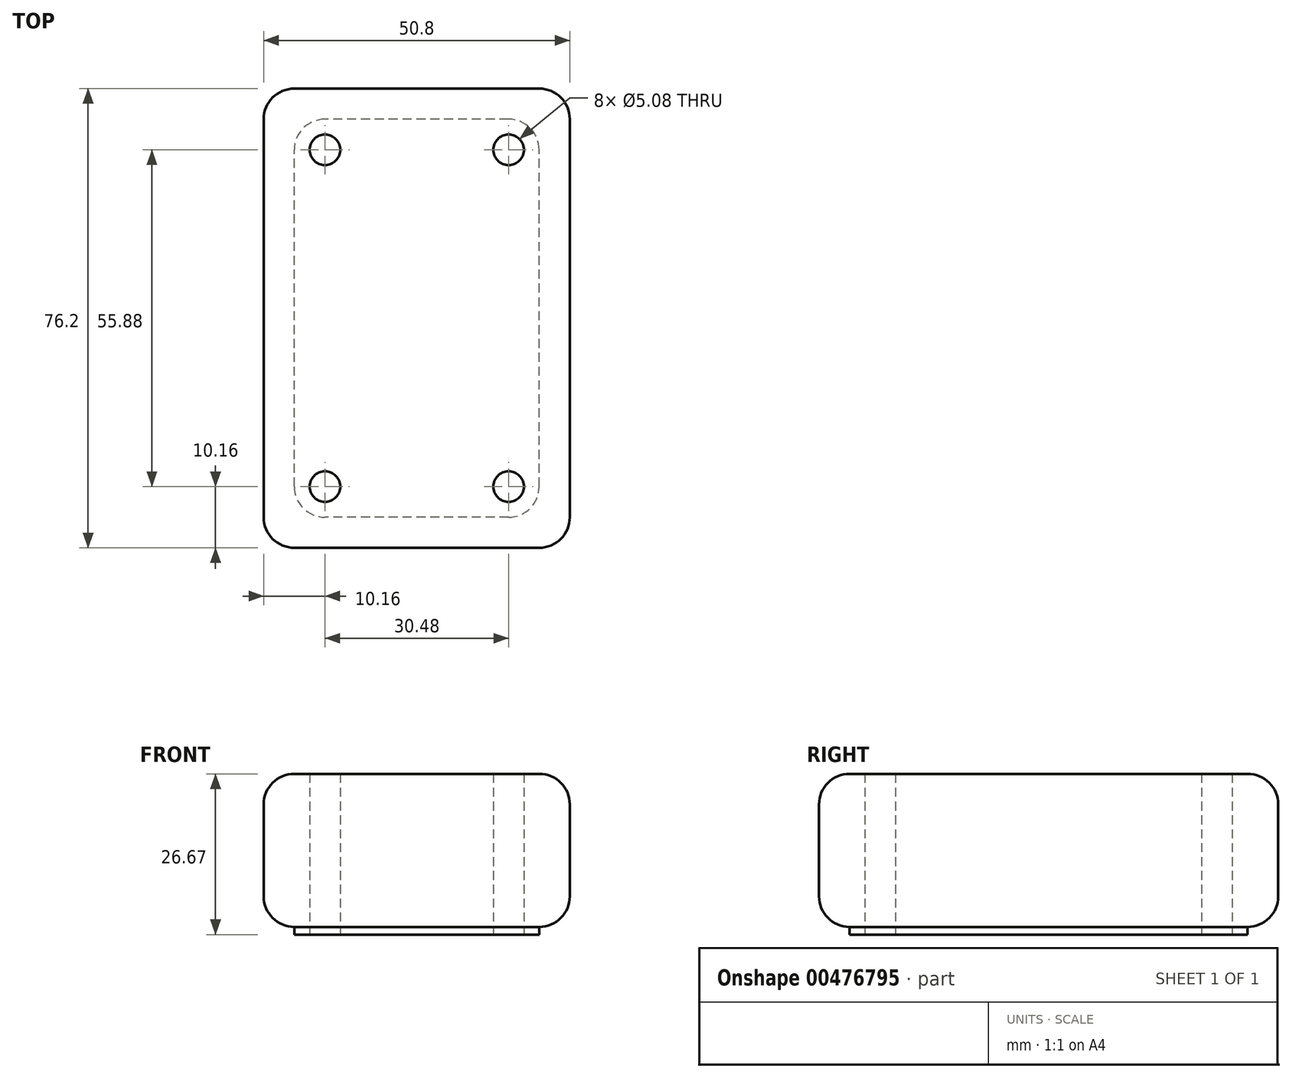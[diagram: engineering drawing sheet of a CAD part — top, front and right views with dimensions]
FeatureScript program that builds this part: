
annotation { "Feature Type Name" : "Feature", "Feature Type Description" : "" }
export const myFeature = defineFeature(function(context is Context, id is Id, definition is map)
    precondition{}
    {
        {
            var Q0;
            Q0=qCreatedBy(makeId("Front.planeOp"),FACE);
            var sketch = newSketch(context, id + "F0", { "sketchPlane" : qUnion([Q0])});
            skLineSegment(sketch, "E0.bottom", {"start": v(25.4, 12.7) * mm, "end": v(-25.4, 12.7) * mm});
            skLineSegment(sketch, "E0.top", {"start": v(25.4, -12.7) * mm, "end": v(-25.4, -12.7) * mm});
            skLineSegment(sketch, "E0.left", {"start": v(25.4, 12.7) * mm, "end": v(25.4, -12.7) * mm});
            skLineSegment(sketch, "E0.right", {"start": v(-25.4, 12.7) * mm, "end": v(-25.4, -12.7) * mm});
            skPoint(sketch, "E0.middle", {"position": v(0, 0) * mm});
            skSolve(sketch);
        }
        {
            var Q0;
            Q0 = qSketchRegion(id + "F0", true);
            extrude(context, id + "F1", {"entities" : qUnion([Q0]), "depth" : 76.2 * mm});
        }
        {
            var Q0;
            Q0=makeQuery(id+"F1.opExtrude","SWEPT_EDGE",EDGE,{"disambiguationData":[OSD([sQuery(id+"F0.wireOp",EDGE,"E0.bottom"),sQuery(id+"F0.wireOp",EDGE,"E0.left")])]});
            var Q1;
            Q1=makeQuery(id+"F1.opExtrude","CAP_EDGE",EDGE,{"disambiguationData":[OSD([sQuery(id+"F0.wireOp",EDGE,"E0.bottom")])],"isStart":true});
            var Q2;
            Q2=makeQuery(id+"F1.opExtrude","SWEPT_EDGE",EDGE,{"disambiguationData":[OSD([sQuery(id+"F0.wireOp",EDGE,"E0.bottom"),sQuery(id+"F0.wireOp",EDGE,"E0.right")])]});
            var Q3;
            Q3=makeQuery(id+"F1.opExtrude","SWEPT_EDGE",EDGE,{"disambiguationData":[OSD([sQuery(id+"F0.wireOp",EDGE,"E0.top"),sQuery(id+"F0.wireOp",EDGE,"E0.left")])]});
            var Q4;
            Q4=makeQuery(id+"F1.opExtrude","SWEPT_EDGE",EDGE,{"disambiguationData":[OSD([sQuery(id+"F0.wireOp",EDGE,"E0.top"),sQuery(id+"F0.wireOp",EDGE,"E0.right")])]});
            var Q5;
            Q5=makeQuery(id+"F1.opExtrude","CAP_EDGE",EDGE,{"disambiguationData":[OSD([sQuery(id+"F0.wireOp",EDGE,"E0.top")])],"isStart":true});
            fillet(context, id + "F2", {"entities" : qUnion([Q0, Q1, Q2, Q3, Q4, Q5]), "radius" : 5.08 * mm, "tangentPropagation" : true, "allowEdgeOverflow" : false});
        }
        {
            var Q0;
            {var subQ0=sQuery(id+"F0.wireOp",EDGE,"E0.bottom");Q0=makeQuery(id+"F2.opFillet","BLEND_EDGE",EDGE,{"blendedFrom":[makeQuery(id+"F1.opExtrude","CAP_EDGE",EDGE,{"disambiguationData":[OSD([subQ0])],"isStart":true}),makeQuery(id+"F1.opExtrude","SWEPT_EDGE",EDGE,{"disambiguationData":[OSD([subQ0,sQuery(id+"F0.wireOp",EDGE,"E0.left")])]})],"blendedInto":[]});}
            var Q1;
            {var subQ0=sQuery(id+"F0.wireOp",EDGE,"E0.bottom");Q1=makeQuery(id+"F2.opFillet","BLEND_EDGE",EDGE,{"blendedFrom":[makeQuery(id+"F1.opExtrude","SWEPT_EDGE",EDGE,{"disambiguationData":[OSD([subQ0,sQuery(id+"F0.wireOp",EDGE,"E0.right")])]}),makeQuery(id+"F1.opExtrude","CAP_EDGE",EDGE,{"disambiguationData":[OSD([subQ0])],"isStart":true})],"blendedInto":[]});}
            var Q2;
            {var subQ0=sQuery(id+"F0.wireOp",EDGE,"E0.bottom");Q2=makeQuery(id+"F2.opFillet","BLEND_EDGE",EDGE,{"blendedFrom":[makeQuery(id+"F1.opExtrude","SWEPT_EDGE",EDGE,{"disambiguationData":[OSD([subQ0,sQuery(id+"F0.wireOp",EDGE,"E0.right")])]}),makeQuery(id+"F1.opExtrude","CAP_EDGE",EDGE,{"disambiguationData":[OSD([subQ0])],"isStart":false})],"blendedInto":[]});}
            fillet(context, id + "F3", {"entities" : qUnion([Q0, Q1, Q2]), "radius" : 5.08 * mm, "tangentPropagation" : true, "allowEdgeOverflow" : false});
        }
        {
            var Q0;
            {var subQ0=sQuery(id+"F0.wireOp",EDGE,"E0.left");var subQ1=sQuery(id+"F0.wireOp",EDGE,"E0.bottom");Q0=makeQuery(id+"F2.opFillet","BLEND_EDGE",EDGE,{"blendedFrom":[makeQuery(id+"F1.opExtrude","SWEPT_EDGE",EDGE,{"disambiguationData":[OSD([subQ1,subQ0])]}),makeQuery(id+"F1.opExtrude","CAP_FACE",FACE,{"disambiguationData":[OSD([subQ1,sQuery(id+"F0.wireOp",EDGE,"E0.top"),subQ0,sQuery(id+"F0.wireOp",EDGE,"E0.right")])],"isStart":false})],"blendedInto":[makeQuery(id+"F1.opExtrude","CAP_FACE",FACE,{"disambiguationData":[OSD([subQ1,sQuery(id+"F0.wireOp",EDGE,"E0.top"),subQ0,sQuery(id+"F0.wireOp",EDGE,"E0.right")])],"isStart":false})]});}
            fillet(context, id + "F4", {"entities" : qUnion([Q0]), "radius" : 5.08 * mm, "tangentPropagation" : true, "allowEdgeOverflow" : false});
        }
        {
            var Q0;
            Q0=makeQuery(id+"F1.opExtrude","SWEPT_FACE",FACE,{"disambiguationData":[OSD([sQuery(id+"F0.wireOp",EDGE,"E0.top")])]});
            var sketch = newSketch(context, id + "F5", { "sketchPlane" : qUnion([Q0])});
            skLineSegment(sketch, "E1.0", {"start": v(-20.32, 5.08) * mm, "end": v(20.32, 5.08) * mm});
            skLineSegment(sketch, "E2.0", {"start": v(20.32, 5.08) * mm, "end": v(20.32, 71.12) * mm});
            skLineSegment(sketch, "E3.0", {"start": v(20.32, 71.12) * mm, "end": v(-20.32, 71.12) * mm});
            skLineSegment(sketch, "E4.0", {"start": v(-20.32, 71.12) * mm, "end": v(-20.32, 5.08) * mm});
            skSolve(sketch);
        }
        {
            var Q0;
            Q0 = qSketchRegion(id + "F5", true);
            extrude(context, id + "F6", {"entities" : qUnion([Q0]), "depth" : 1.27 * mm});
        }
        {
            var Q0;
            Q0=makeQuery(id+"F6.opExtrude","SWEPT_EDGE",EDGE,{"disambiguationData":[OSD([sQuery(id+"F5.wireOp",EDGE,"E1.0"),sQuery(id+"F5.wireOp",EDGE,"E4.0")])]});
            var Q1;
            Q1=makeQuery(id+"F6.opExtrude","SWEPT_EDGE",EDGE,{"disambiguationData":[OSD([sQuery(id+"F5.wireOp",EDGE,"E1.0"),sQuery(id+"F5.wireOp",EDGE,"E2.0")])]});
            var Q2;
            Q2=makeQuery(id+"F6.opExtrude","SWEPT_EDGE",EDGE,{"disambiguationData":[OSD([sQuery(id+"F5.wireOp",EDGE,"E2.0"),sQuery(id+"F5.wireOp",EDGE,"E3.0")])]});
            var Q3;
            Q3=makeQuery(id+"F6.opExtrude","SWEPT_EDGE",EDGE,{"disambiguationData":[OSD([sQuery(id+"F5.wireOp",EDGE,"E3.0"),sQuery(id+"F5.wireOp",EDGE,"E4.0")])]});
            fillet(context, id + "F7", {"entities" : qUnion([Q0, Q1, Q2, Q3]), "radius" : 5.08 * mm, "tangentPropagation" : true, "allowEdgeOverflow" : false});
        }
        {
            var Q0;
            Q0=makeQuery(id+"F6.opExtrude","CAP_FACE",FACE,{"disambiguationData":[OSD([sQuery(id+"F5.wireOp",EDGE,"E1.0"),sQuery(id+"F5.wireOp",EDGE,"E2.0"),sQuery(id+"F5.wireOp",EDGE,"E3.0"),sQuery(id+"F5.wireOp",EDGE,"E4.0")])],"isStart":false});
            var sketch = newSketch(context, id + "F8", { "sketchPlane" : qUnion([Q0])});
            skLineSegment(sketch, "E5", {"start": v(20.32, 10.16) * mm, "end": v(-20.32, 10.16) * mm, "construction": true});
            skLineSegment(sketch, "E6", {"start": v(15.24, 5.08) * mm, "end": v(15.24, 71.12) * mm, "construction": true});
            skLineSegment(sketch, "E7", {"start": v(20.32, 66.04) * mm, "end": v(-20.32, 66.04) * mm, "construction": true});
            skLineSegment(sketch, "E8", {"start": v(-15.24, 71.12) * mm, "end": v(-15.24, 5.08) * mm, "construction": true});
            skCircle(sketch, "E9", {"center": v(15.24, 10.16) * mm, "radius": 2.54 * mm});
            skCircle(sketch, "E10", {"center": v(15.24, 66.04) * mm, "radius": 2.54 * mm});
            skCircle(sketch, "E11", {"center": v(-15.24, 66.04) * mm, "radius": 2.54 * mm});
            skCircle(sketch, "E12", {"center": v(-15.24, 10.16) * mm, "radius": 2.54 * mm});
            skSolve(sketch);
        }
        {
            var Q0;
            Q0 = qSketchRegion(id + "F8", true);
            extrude(context, id + "F9", {"entities" : qUnion([Q0]), "operationType" : NewBodyOperationType.REMOVE, "oppositeDirection" : true, "depth" : 101.6 * mm});
        }
        {
            var Q0;
            Q0=makeQuery(id+"F1.opExtrude","SWEPT_FACE",FACE,{"disambiguationData":[OSD([sQuery(id+"F0.wireOp",EDGE,"E0.top")])]});
            var sketch = newSketch(context, id + "F10", { "sketchPlane" : qUnion([Q0])});
            skCircle(sketch, "E13.0", {"center": v(15.24, 66.04) * mm, "radius": 2.54 * mm});
            skCircle(sketch, "E14.0", {"center": v(-15.24, 66.04) * mm, "radius": 2.54 * mm});
            skCircle(sketch, "E15.0", {"center": v(15.24, 10.16) * mm, "radius": 2.54 * mm});
            skCircle(sketch, "E16.0", {"center": v(-15.24, 10.16) * mm, "radius": 2.54 * mm});
            skSolve(sketch);
        }
        {
            var Q0;
            Q0 = qSketchRegion(id + "F10", true);
            extrude(context, id + "F11", {"entities" : qUnion([Q0]), "operationType" : NewBodyOperationType.REMOVE, "oppositeDirection" : true, "depth" : 101.6 * mm});
        }
    });
